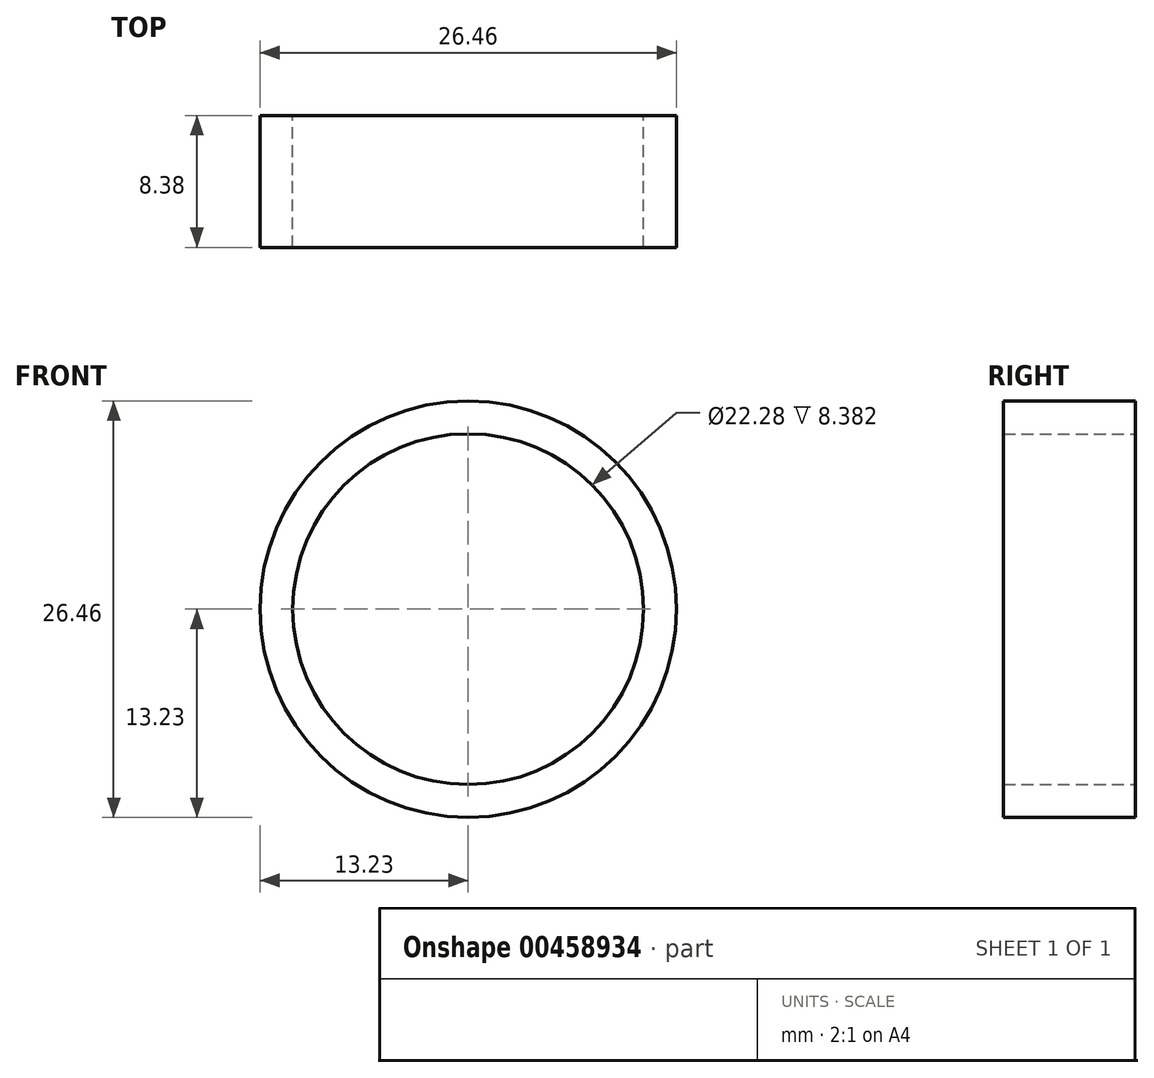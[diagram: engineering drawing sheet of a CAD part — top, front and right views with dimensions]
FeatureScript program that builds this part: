
annotation { "Feature Type Name" : "Feature", "Feature Type Description" : "" }
export const myFeature = defineFeature(function(context is Context, id is Id, definition is map)
    precondition{}
    {
        {
            var Q0;
            Q0=qCreatedBy(makeId("Front.planeOp"),FACE);
            var sketch = newSketch(context, id + "F0", { "sketchPlane" : qUnion([Q0])});
            skLineSegment(sketch, "E0", {"start": v(0, 0) * mm, "end": v(0, 2.54) * mm});
            skLineSegment(sketch, "E1", {"start": v(0, 2.54) * mm, "end": v(1.5, 2.54) * mm});
            skLineSegment(sketch, "E2", {"start": v(1.5, 2.54) * mm, "end": v(1.5, 0) * mm});
            skLineSegment(sketch, "E3", {"start": v(1.5, 0) * mm, "end": v(0, 0) * mm});
            skSolve(sketch);
        }
        {
            var Q0;
            Q0=qCreatedBy(makeId("Front.planeOp"),FACE);
            var sketch = newSketch(context, id + "F1", { "sketchPlane" : qUnion([Q0])});
            skCircle(sketch, "E4", {"center": v(0, 0) * mm, "radius": 13.23 * mm});
            skCircle(sketch, "E5", {"center": v(0, 0) * mm, "radius": 11.14 * mm});
            skSolve(sketch);
        }
        {
            var Q0;
            Q0=makeQuery(id+"F1.imprint","IMPRINT",FACE,{"disambiguationData":[TD([[makeQuery(id+"F1.imprint","IMPRINT",EDGE,{"derivedFrom":sQuery(id+"F1.wireOp",EDGE,"E4")}),1.0]])]});
            extrude(context, id + "F2", {"entities" : qUnion([Q0]), "depth" : 8.38 * mm});
        }
    });
